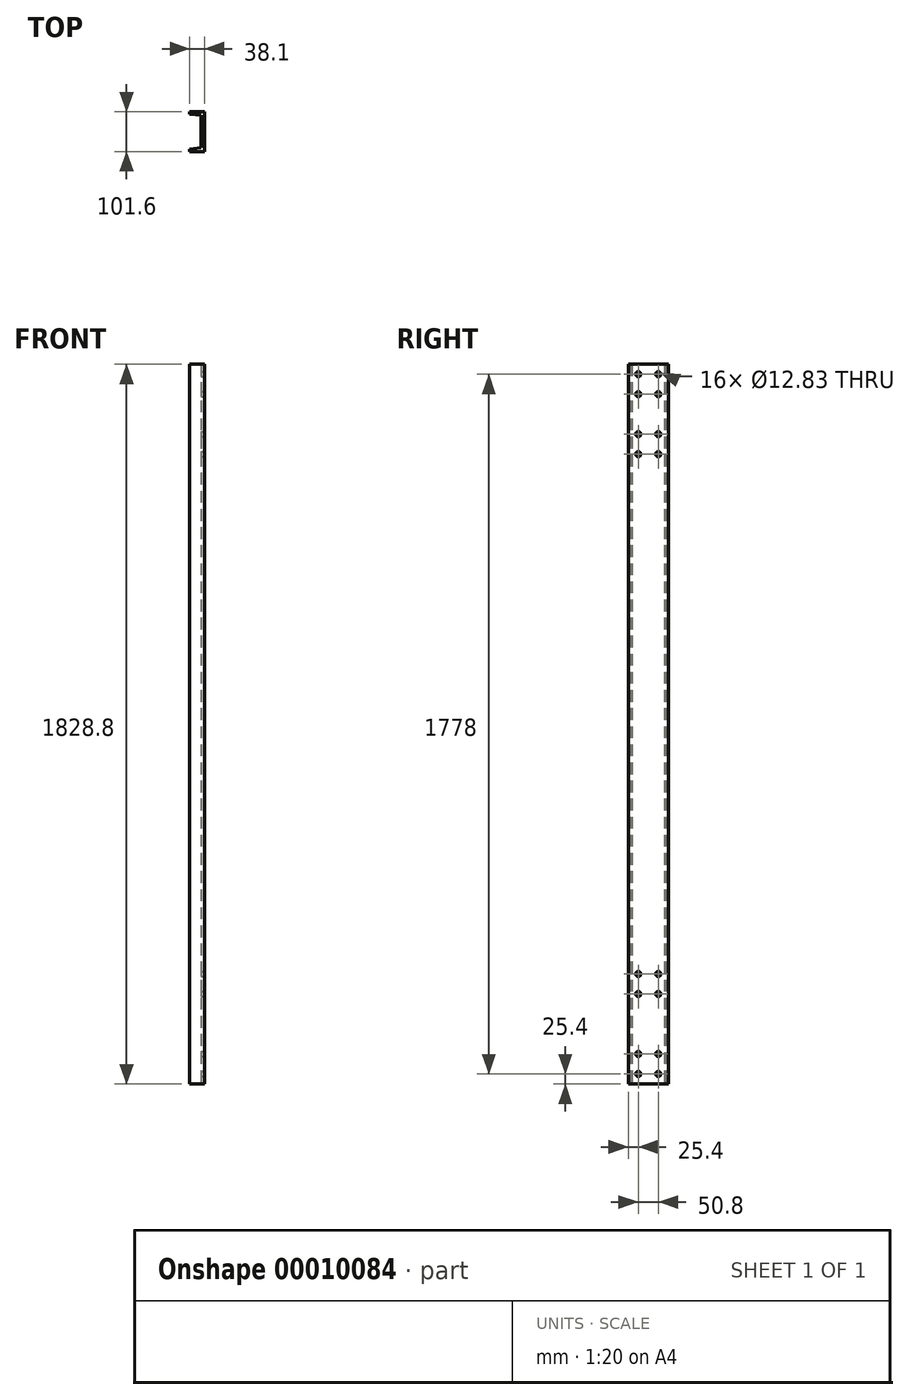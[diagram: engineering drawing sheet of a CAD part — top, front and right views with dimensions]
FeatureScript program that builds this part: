
annotation { "Feature Type Name" : "Feature", "Feature Type Description" : "" }
export const myFeature = defineFeature(function(context is Context, id is Id, definition is map)
    precondition{}
    {
        {
            var Q0;
            Q0=qCreatedBy(makeId("Top.planeOp"),FACE);
            var sketch = newSketch(context, id + "F0", { "sketchPlane" : qUnion([Q0])});
            skLineSegment(sketch, "E0", {"start": v(-38.1, 50.8) * mm, "end": v(0, 50.8) * mm});
            skLineSegment(sketch, "E1", {"start": v(0, 50.8) * mm, "end": v(0, 0) * mm});
            skLineSegment(sketch, "E2", {"start": v(0, 0) * mm, "end": v(0, -50.8) * mm});
            skLineSegment(sketch, "E3", {"start": v(0, -50.8) * mm, "end": v(-38.1, -50.8) * mm});
            skLineSegment(sketch, "E4", {"start": v(-38.1, -50.8) * mm, "end": v(-38.1, -44.45) * mm});
            skLineSegment(sketch, "E5", {"start": v(-38.1, -44.45) * mm, "end": v(-9.52, -41.27) * mm});
            skLineSegment(sketch, "E6", {"start": v(-9.52, 41.28) * mm, "end": v(-38.1, 44.45) * mm});
            skLineSegment(sketch, "E7", {"start": v(-38.1, 44.45) * mm, "end": v(-38.1, 50.8) * mm});
            skLineSegment(sketch, "E8", {"start": v(-9.52, -41.27) * mm, "end": v(-9.53, 0) * mm});
            skLineSegment(sketch, "E9", {"start": v(-9.53, 0) * mm, "end": v(-9.53, 41.27) * mm});
            skSolve(sketch);
        }
        {
            var Q0;
            Q0 = qSketchRegion(id + "F0", true);
            extrude(context, id + "F1", {"entities" : qUnion([Q0]), "depth" : 1828.8 * mm});
        }
        {
            var Q0;
            Q0=makeQuery(id+"F1.opExtrude","SWEPT_FACE",FACE,{"disambiguationData":[OSD([sQuery(id+"F0.wireOp",EDGE,"E1"),sQuery(id+"F0.wireOp",EDGE,"E2")])]});
            var sketch = newSketch(context, id + "F2", { "sketchPlane" : qUnion([Q0])});
            skCircle(sketch, "E10", {"center": v(-25.4, 25.4) * mm, "radius": 6.41 * mm});
            skCircle(sketch, "E11", {"center": v(-25.4, 76.2) * mm, "radius": 6.41 * mm});
            skCircle(sketch, "E12", {"center": v(25.4, 76.2) * mm, "radius": 6.41 * mm});
            skCircle(sketch, "E13", {"center": v(25.4, 25.4) * mm, "radius": 6.41 * mm});
            skLineSegment(sketch, "E14", {"start": v(-25.4, 25.4) * mm, "end": v(25.4, 25.4) * mm});
            skLineSegment(sketch, "E15", {"start": v(0, 25.4) * mm, "end": v(0, 0) * mm});
            skCircle(sketch, "E16", {"center": v(-25.4, 1803.4) * mm, "radius": 6.41 * mm});
            skCircle(sketch, "E17", {"center": v(25.4, 1803.4) * mm, "radius": 6.41 * mm});
            skCircle(sketch, "E18", {"center": v(-25.4, 1752.6) * mm, "radius": 6.41 * mm});
            skCircle(sketch, "E19", {"center": v(25.4, 1752.6) * mm, "radius": 6.41 * mm});
            skLineSegment(sketch, "E20", {"start": v(-25.4, 1803.4) * mm, "end": v(25.4, 1803.4) * mm});
            skLineSegment(sketch, "E21", {"start": v(0, 1803.4) * mm, "end": v(0, 1828.8) * mm});
            skCircle(sketch, "E22", {"center": v(-25.4, 1651) * mm, "radius": 6.41 * mm});
            skCircle(sketch, "E23", {"center": v(25.4, 1651) * mm, "radius": 6.41 * mm});
            skCircle(sketch, "E24", {"center": v(-25.4, 1600.2) * mm, "radius": 6.41 * mm});
            skCircle(sketch, "E25", {"center": v(25.4, 1600.2) * mm, "radius": 6.41 * mm});
            skCircle(sketch, "E26", {"center": v(-25.4, 279.4) * mm, "radius": 6.41 * mm});
            skCircle(sketch, "E27", {"center": v(-25.4, 228.6) * mm, "radius": 6.41 * mm});
            skCircle(sketch, "E28", {"center": v(25.4, 279.4) * mm, "radius": 6.41 * mm});
            skCircle(sketch, "E29", {"center": v(25.4, 228.6) * mm, "radius": 6.41 * mm});
            skSolve(sketch);
        }
        {
            var Q0;
            Q0 = qSketchRegion(id + "F2", true);
            extrude(context, id + "F3", {"entities" : qUnion([Q0]), "operationType" : NewBodyOperationType.REMOVE, "endBound" : BoundingType.THROUGH_ALL, "oppositeDirection" : true, "depth" : 25.4 * mm});
        }
    });
